# Revit family: Flush_Valve-Clinic_Sink-American_Standard-Ultima_Sensor-6147SM117.002
name_source: partatom
category: Plumbing Fixtures
revit_build: Autodesk Revit 2014 (Build: 20130308_1515(x64)
units: mm (PartAtom-declared; Revit-internal decimal feet)

## types (1)
- 6147SM117.002
    ADA Compliant = Yes
    Assembly Code = D2020300
    CW Connection = Yes
    CWFU = 10
    Cold Water Connection Diameter = 1"
    Cold Water Connection Height = 24"
    Cold Water Connection Radius = 1/2"
    Cold Water Connection Width = 4 1/4"
    Default Elevation = 0"
    Description = Ultima Sensor-Operated Clinic Sink Flush Valve Diaphragm-Type
    Finish = Brass-American Standard-002-Polished Chrome
    Flush Rate = 6.5 gpf (24.6 Lpf)
    HW Connection = No
    HWFU = 0
    Height = 27 1/8"
    Manufacturer = American Standard
    Material = Brass-American Standard-002-Polished Chrome
    Model = 6147SM117.002
    Price = Prices may vary. Please consult Manufacturer Representative for most up-to-date price list.
    URL = https://www.americanstandard-us.com
    Vent Connection = No
    WFU = 0
    Warranty Information = 1 Year Limited Warranty
    Waste Connection = No

## geometry (parser evidence)
native form markers: Sweep x1
no freeform markers — native parametric forms only
